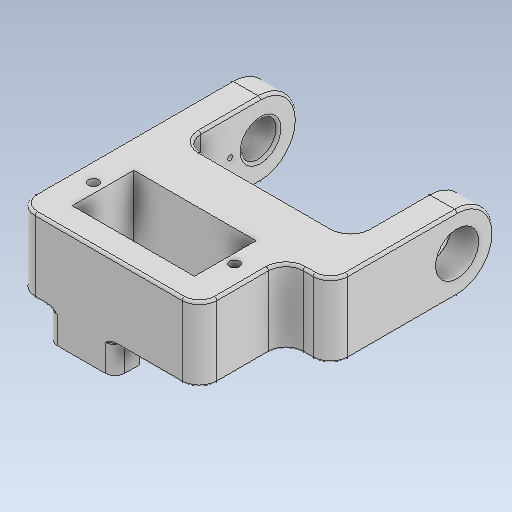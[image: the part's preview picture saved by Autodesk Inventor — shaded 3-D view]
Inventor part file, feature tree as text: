
AUTODESK INVENTOR PART (.ipt)
format: ipt  version: 2020.3 (Build 243373000, 373)  size: 307,200 bytes
history: native  units: mm
features: sketch x5, other x3
ambient origin geometry x8: Origin, YZ Plane, XZ Plane, XY Plane, X Axis, Y Axis, Z Axis, Center Point
bodies: Solid1 (feature_tree)
feature tree (8):
  other  "LegStart_v1.ipt"
  other  "Solid1::LegStart_v1.ipt"
  other  "TaggingFeature1"
  sketch  "Sketch1"  dims[d0=10.0mm]
  sketch  "Sketch2"
  sketch  "Sketch3"
  sketch  "Sketch8"
  sketch  "Sketch9"
